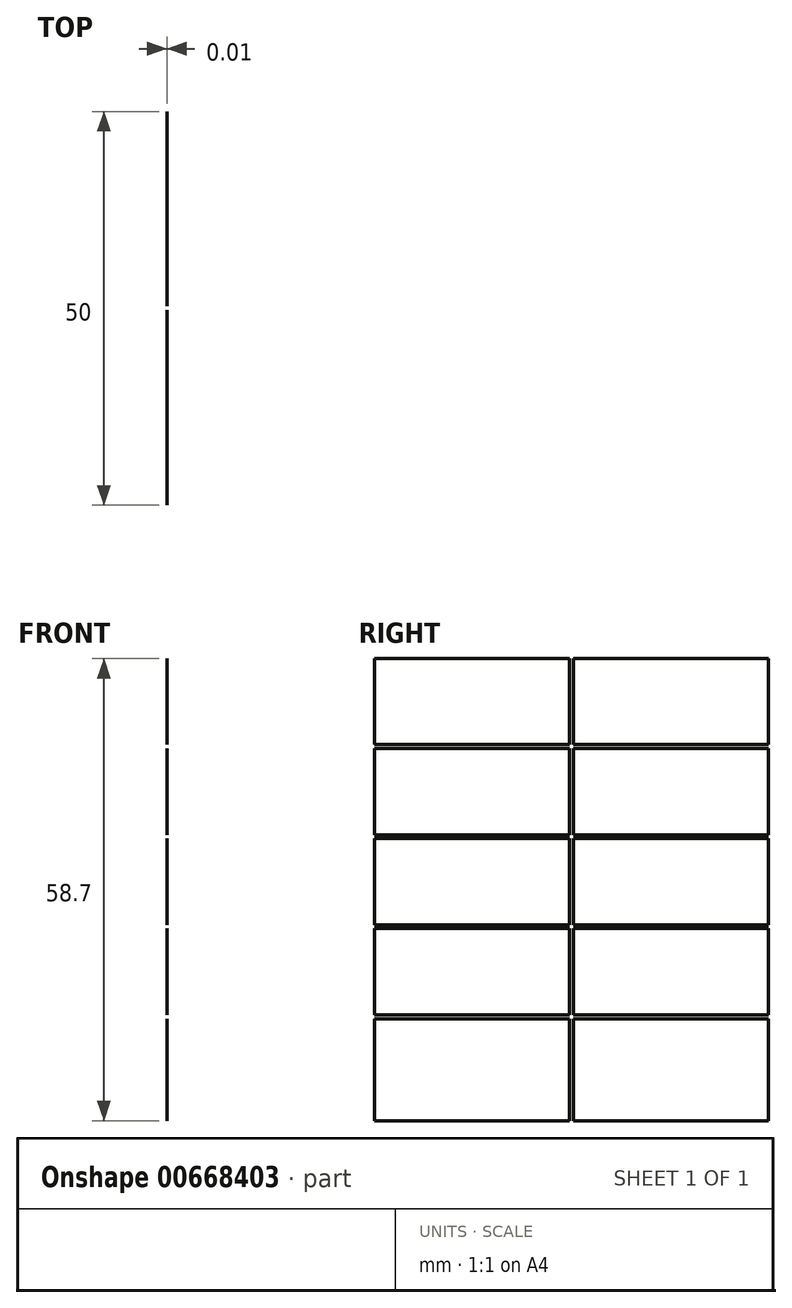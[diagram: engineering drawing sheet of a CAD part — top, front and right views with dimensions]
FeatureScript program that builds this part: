
annotation { "Feature Type Name" : "Feature", "Feature Type Description" : "" }
export const myFeature = defineFeature(function(context is Context, id is Id, definition is map)
    precondition{}
    {
        {
            var Q0;
            Q0=qCreatedBy(makeId("Right.planeOp"),FACE);
            var sketch = newSketch(context, id + "F0", { "sketchPlane" : qUnion([Q0])});
            skPoint(sketch, "E0.0", {"position": v(0, 0) * mm});
            skLineSegment(sketch, "E1.bottom", {"start": v(0, 0) * mm, "end": v(50, 0) * mm});
            skLineSegment(sketch, "E1.top", {"start": v(0, -60) * mm, "end": v(50, -60) * mm});
            skLineSegment(sketch, "E1.left", {"start": v(0, 0) * mm, "end": v(0, -12.24) * mm});
            skLineSegment(sketch, "E1.right", {"start": v(50, 0) * mm, "end": v(50, -12.24) * mm});
            skPoint(sketch, "E2.MirrorP", {"position": v(11.5, 0) * mm});
            skPoint(sketch, "E3.MirrorP", {"position": v(18.5, 0) * mm});
            skPoint(sketch, "E4.MirrorP", {"position": v(30, 0) * mm});
            skLineSegment(sketch, "E5.0", {"start": v(25.25, -60) * mm, "end": v(25.25, -52.76) * mm});
            skLineSegment(sketch, "E6.0", {"start": v(24.75, -60) * mm, "end": v(24.75, -52.76) * mm});
            skLineSegment(sketch, "E7.0", {"start": v(0, -1.3) * mm, "end": v(24.75, -1.3) * mm});
            skLineSegment(sketch, "E8.trimOffspring", {"start": v(25.25, -1.3) * mm, "end": v(50, -1.3) * mm});
            skLineSegment(sketch, "E9.0", {"start": v(0, -12.24) * mm, "end": v(24.75, -12.24) * mm});
            skLineSegment(sketch, "E10.0", {"start": v(0, -12.74) * mm, "end": v(24.75, -12.74) * mm});
            skLineSegment(sketch, "E11.trimOffspring", {"start": v(25.25, -6.52) * mm, "end": v(25.25, -1.3) * mm});
            skLineSegment(sketch, "E12.trimOffspring", {"start": v(24.75, -6.52) * mm, "end": v(24.75, -1.3) * mm});
            skLineSegment(sketch, "E13.trimOffspring", {"start": v(25.25, -12.24) * mm, "end": v(50, -12.24) * mm});
            skLineSegment(sketch, "E14.trimOffspring", {"start": v(25.25, -12.24) * mm, "end": v(25.25, -7.02) * mm});
            skLineSegment(sketch, "E15.trimOffspring", {"start": v(24.75, -12.24) * mm, "end": v(24.75, -7.02) * mm});
            skLineSegment(sketch, "E16.trimOffspring", {"start": v(25.25, -12.74) * mm, "end": v(50, -12.74) * mm});
            skLineSegment(sketch, "E17.trimOffspring", {"start": v(24.75, -17.95) * mm, "end": v(24.75, -12.74) * mm});
            skLineSegment(sketch, "E18.trimOffspring", {"start": v(25.25, -17.95) * mm, "end": v(25.25, -12.74) * mm});
            skLineSegment(sketch, "E19.0", {"start": v(0, -23.67) * mm, "end": v(24.75, -23.67) * mm});
            skLineSegment(sketch, "E20.0", {"start": v(0, -24.17) * mm, "end": v(24.75, -24.17) * mm});
            skLineSegment(sketch, "E21.trimOffspring", {"start": v(25.25, -23.67) * mm, "end": v(50, -23.67) * mm});
            skLineSegment(sketch, "E22.trimOffspring", {"start": v(25.25, -23.67) * mm, "end": v(25.25, -18.45) * mm});
            skLineSegment(sketch, "E23.trimOffspring", {"start": v(24.75, -23.67) * mm, "end": v(24.75, -18.45) * mm});
            skLineSegment(sketch, "E24.trimOffspring", {"start": v(25.25, -24.17) * mm, "end": v(50, -24.17) * mm});
            skLineSegment(sketch, "E25.trimOffspring", {"start": v(25.25, -29.39) * mm, "end": v(25.25, -24.17) * mm});
            skLineSegment(sketch, "E26.trimOffspring", {"start": v(24.75, -29.39) * mm, "end": v(24.75, -24.17) * mm});
            skLineSegment(sketch, "E27.0", {"start": v(0, -35.1) * mm, "end": v(24.75, -35.1) * mm});
            skLineSegment(sketch, "E28.0", {"start": v(0, -35.6) * mm, "end": v(24.75, -35.6) * mm});
            skLineSegment(sketch, "E29.trimOffspring", {"start": v(25.25, -35.1) * mm, "end": v(50, -35.1) * mm});
            skLineSegment(sketch, "E30.trimOffspring", {"start": v(25.25, -35.1) * mm, "end": v(25.25, -29.89) * mm});
            skLineSegment(sketch, "E31.trimOffspring", {"start": v(24.75, -35.1) * mm, "end": v(24.75, -29.89) * mm});
            skLineSegment(sketch, "E32.trimOffspring", {"start": v(25.25, -35.6) * mm, "end": v(50, -35.6) * mm});
            skLineSegment(sketch, "E33.trimOffspring", {"start": v(25.25, -40.82) * mm, "end": v(25.25, -35.6) * mm});
            skLineSegment(sketch, "E34.trimOffspring", {"start": v(24.75, -40.82) * mm, "end": v(24.75, -35.6) * mm});
            skLineSegment(sketch, "E35.0", {"start": v(0, -46.54) * mm, "end": v(24.75, -46.54) * mm});
            skLineSegment(sketch, "E36.0", {"start": v(0, -47.04) * mm, "end": v(24.75, -47.04) * mm});
            skLineSegment(sketch, "E37.trimOffspring", {"start": v(25.25, -46.54) * mm, "end": v(50, -46.54) * mm});
            skLineSegment(sketch, "E38.trimOffspring", {"start": v(25.25, -46.54) * mm, "end": v(25.25, -41.32) * mm});
            skLineSegment(sketch, "E39.trimOffspring", {"start": v(24.75, -46.54) * mm, "end": v(24.75, -41.32) * mm});
            skLineSegment(sketch, "E40.trimOffspring", {"start": v(25.25, -47.04) * mm, "end": v(50, -47.04) * mm});
            skLineSegment(sketch, "E41.trimOffspring", {"start": v(25.25, -52.26) * mm, "end": v(25.25, -47.04) * mm});
            skLineSegment(sketch, "E42.trimOffspring", {"start": v(24.75, -52.26) * mm, "end": v(24.75, -47.04) * mm});
            skLineSegment(sketch, "E43", {"start": v(24.75, -6.52) * mm, "end": v(24.75, -7.02) * mm});
            skLineSegment(sketch, "E44", {"start": v(25.25, -6.52) * mm, "end": v(25.25, -7.02) * mm});
            skLineSegment(sketch, "E45", {"start": v(24.75, -17.95) * mm, "end": v(24.75, -18.45) * mm});
            skLineSegment(sketch, "E46", {"start": v(25.25, -17.95) * mm, "end": v(25.25, -18.45) * mm});
            skLineSegment(sketch, "E47", {"start": v(25.25, -29.39) * mm, "end": v(25.25, -29.89) * mm});
            skLineSegment(sketch, "E48", {"start": v(24.75, -29.39) * mm, "end": v(24.75, -29.89) * mm});
            skLineSegment(sketch, "E49", {"start": v(25.25, -40.82) * mm, "end": v(25.25, -41.32) * mm});
            skLineSegment(sketch, "E50", {"start": v(24.75, -40.82) * mm, "end": v(24.75, -41.32) * mm});
            skLineSegment(sketch, "E51", {"start": v(24.75, -52.26) * mm, "end": v(24.75, -52.76) * mm});
            skLineSegment(sketch, "E52", {"start": v(25.25, -52.26) * mm, "end": v(25.25, -52.76) * mm});
            skLineSegment(sketch, "E53.trimOffspring", {"start": v(0, -12.74) * mm, "end": v(0, -23.67) * mm});
            skLineSegment(sketch, "E54.trimOffspring", {"start": v(0, -24.17) * mm, "end": v(0, -35.1) * mm});
            skLineSegment(sketch, "E55.trimOffspring", {"start": v(0, -35.6) * mm, "end": v(0, -46.54) * mm});
            skLineSegment(sketch, "E56.trimOffspring", {"start": v(0, -47.04) * mm, "end": v(0, -60) * mm});
            skLineSegment(sketch, "E57.trimOffspring", {"start": v(50, -47.04) * mm, "end": v(50, -60) * mm});
            skLineSegment(sketch, "E58.trimOffspring", {"start": v(50, -35.6) * mm, "end": v(50, -46.54) * mm});
            skLineSegment(sketch, "E59.trimOffspring", {"start": v(50, -12.74) * mm, "end": v(50, -23.67) * mm});
            skLineSegment(sketch, "E60.trimOffspring", {"start": v(50, -24.17) * mm, "end": v(50, -35.1) * mm});
            skSolve(sketch);
        }
        {
            var Q0;
            {var subQ1=sQuery(id+"F0.wireOp",EDGE,"E7.0");Q0=makeQuery(id+"F0.imprint","IMPRINT",FACE,{"disambiguationData":[TD([[makeQuery(id+"F0.imprint","IMPRINT",EDGE,{"derivedFrom":subQ1}),-1.0]])]});}
            var Q1;
            {var subQ1=sQuery(id+"F0.wireOp",EDGE,"E8.trimOffspring");Q1=makeQuery(id+"F0.imprint","IMPRINT",FACE,{"disambiguationData":[TD([[makeQuery(id+"F0.imprint","IMPRINT",EDGE,{"derivedFrom":subQ1}),-1.0]])]});}
            var Q2;
            Q2=makeQuery(id+"F0.imprint","IMPRINT",FACE,{"disambiguationData":[TD([[makeQuery(id+"F0.imprint","IMPRINT",EDGE,{"derivedFrom":sQuery(id+"F0.wireOp",EDGE,"E10.0")}),-1.0]])]});
            var Q3;
            Q3=makeQuery(id+"F0.imprint","IMPRINT",FACE,{"disambiguationData":[TD([[makeQuery(id+"F0.imprint","IMPRINT",EDGE,{"derivedFrom":sQuery(id+"F0.wireOp",EDGE,"E16.trimOffspring")}),-1.0]])]});
            var Q4;
            Q4=makeQuery(id+"F0.imprint","IMPRINT",FACE,{"disambiguationData":[TD([[makeQuery(id+"F0.imprint","IMPRINT",EDGE,{"derivedFrom":sQuery(id+"F0.wireOp",EDGE,"E24.trimOffspring")}),-1.0]])]});
            var Q5;
            Q5=makeQuery(id+"F0.imprint","IMPRINT",FACE,{"disambiguationData":[TD([[makeQuery(id+"F0.imprint","IMPRINT",EDGE,{"derivedFrom":sQuery(id+"F0.wireOp",EDGE,"E20.0")}),-1.0]])]});
            var Q6;
            Q6=makeQuery(id+"F0.imprint","IMPRINT",FACE,{"disambiguationData":[TD([[makeQuery(id+"F0.imprint","IMPRINT",EDGE,{"derivedFrom":sQuery(id+"F0.wireOp",EDGE,"E28.0")}),-1.0]])]});
            var Q7;
            Q7=makeQuery(id+"F0.imprint","IMPRINT",FACE,{"disambiguationData":[TD([[makeQuery(id+"F0.imprint","IMPRINT",EDGE,{"derivedFrom":sQuery(id+"F0.wireOp",EDGE,"E32.trimOffspring")}),-1.0]])]});
            var Q8;
            {var subQ0=sQuery(id+"F0.wireOp",EDGE,"E5.0");Q8=makeQuery(id+"F0.imprint","IMPRINT",FACE,{"disambiguationData":[TD([[makeQuery(id+"F0.imprint","IMPRINT",EDGE,{"derivedFrom":subQ0}),-1.0]])]});}
            var Q9;
            {var subQ0=sQuery(id+"F0.wireOp",EDGE,"E6.0");Q9=makeQuery(id+"F0.imprint","IMPRINT",FACE,{"disambiguationData":[TD([[makeQuery(id+"F0.imprint","IMPRINT",EDGE,{"derivedFrom":subQ0}),1.0]])]});}
            extrude(context, id + "F1", {"entities" : qUnion([Q0, Q1, Q2, Q3, Q4, Q5, Q6, Q7, Q8, Q9]), "depth" : 0.01 * mm, "offsetDistance" : 25 * mm});
        }
    });
